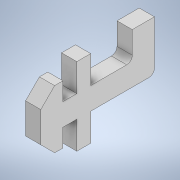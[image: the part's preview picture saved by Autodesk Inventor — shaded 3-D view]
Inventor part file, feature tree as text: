
AUTODESK INVENTOR PART (.ipt)
format: ipt  version: 2020 (Build 240168000, 168)  size: 136,192 bytes
history: native  units: mm
features: extrude x1, fillet x1, sketch x1
ambient origin geometry x8: Origin, YZ Plane, XZ Plane, XY Plane, X Axis, Y Axis, Z Axis, Center Point
bodies: Solide1 (feature_tree)
feature tree (3):
  extrude  "Extrusion1"  Depth=8.0mm
  fillet  "Congé1"  Radius=8.0mm
  sketch  "Esquisse1"
